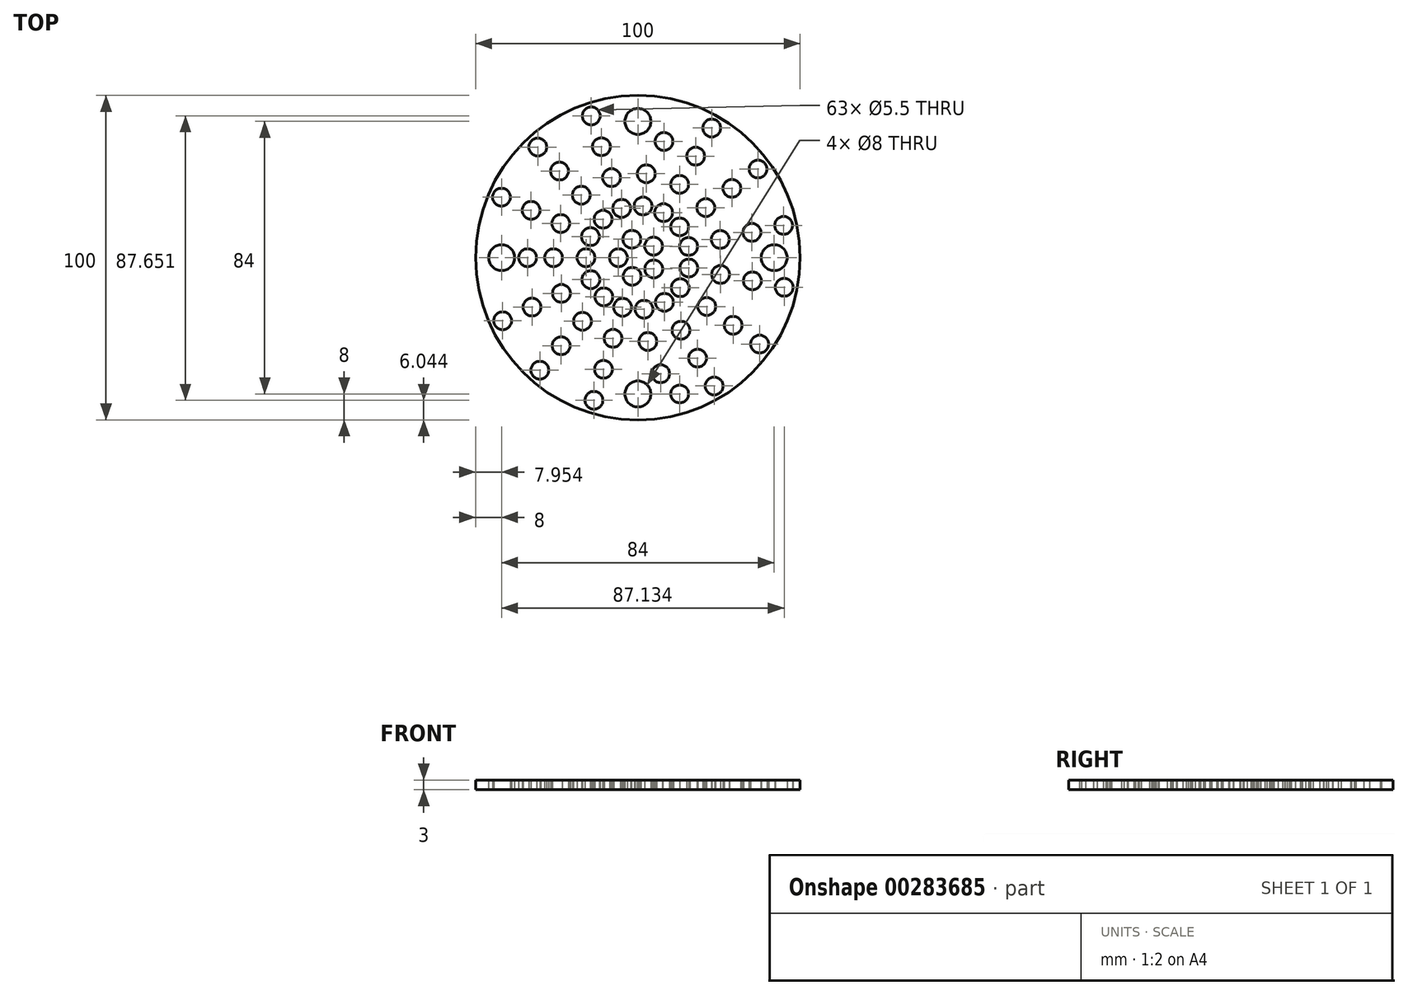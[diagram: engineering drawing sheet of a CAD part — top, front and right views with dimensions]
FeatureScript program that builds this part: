
annotation { "Feature Type Name" : "Feature", "Feature Type Description" : "" }
export const myFeature = defineFeature(function(context is Context, id is Id, definition is map)
    precondition{}
    {
        {
            var Q0;
            Q0=qCreatedBy(makeId("Top.planeOp"),FACE);
            var sketch = newSketch(context, id + "F0", { "sketchPlane" : qUnion([Q0])});
            skCircle(sketch, "E0", {"center": v(0, 0) * mm, "radius": 50 * mm});
            skCircle(sketch, "E1", {"center": v(0, -42) * mm, "radius": 4 * mm});
            skCircle(sketch, "E2.1.0", {"center": v(42, 0) * mm, "radius": 4 * mm});
            skCircle(sketch, "E2.2.0", {"center": v(0, 42) * mm, "radius": 4 * mm});
            skCircle(sketch, "E2.3.0", {"center": v(-42, 0) * mm, "radius": 4 * mm});
            skCircle(sketch, "E3", {"center": v(-6, 0) * mm, "radius": 2.75 * mm});
            skCircle(sketch, "E4.1.0.0", {"center": v(-16, 0) * mm, "radius": 2.75 * mm});
            skCircle(sketch, "E4.2.0.0", {"center": v(-26, 0) * mm, "radius": 2.75 * mm});
            skCircle(sketch, "E4.3.0.0", {"center": v(-34, 0) * mm, "radius": 2.75 * mm});
            skLineSegment(sketch, "E4.direction1", {"start": v(-6, 0) * mm, "end": v(-16, 0) * mm, "construction": true});
            skCircle(sketch, "E5.1.1", {"center": v(-14.62, 6.49) * mm, "radius": 2.75 * mm});
            skCircle(sketch, "E5.1.2", {"center": v(-23.77, 10.55) * mm, "radius": 2.75 * mm});
            skCircle(sketch, "E5.1.3", {"center": v(-32.9, 14.6) * mm, "radius": 2.75 * mm});
            skCircle(sketch, "E5.1.4", {"center": v(-42.05, 18.66) * mm, "radius": 2.75 * mm});
            skCircle(sketch, "E5.2.1", {"center": v(-10.74, 11.86) * mm, "radius": 2.75 * mm});
            skCircle(sketch, "E5.2.2", {"center": v(-17.45, 19.28) * mm, "radius": 2.75 * mm});
            skCircle(sketch, "E5.2.3", {"center": v(-24.16, 26.7) * mm, "radius": 2.75 * mm});
            skCircle(sketch, "E5.2.4", {"center": v(-30.87, 34.1) * mm, "radius": 2.75 * mm});
            skCircle(sketch, "E5.3.0", {"center": v(-1.88, 5.7) * mm, "radius": 2.75 * mm});
            skCircle(sketch, "E5.3.1", {"center": v(-5, 15.2) * mm, "radius": 2.75 * mm});
            skCircle(sketch, "E5.3.2", {"center": v(-8.13, 24.7) * mm, "radius": 2.75 * mm});
            skCircle(sketch, "E5.3.3", {"center": v(-11.25, 34.2) * mm, "radius": 2.75 * mm});
            skCircle(sketch, "E5.3.4", {"center": v(-14.38, 43.7) * mm, "radius": 2.75 * mm});
            skCircle(sketch, "E5.4.1", {"center": v(1.6, 15.92) * mm, "radius": 2.75 * mm});
            skCircle(sketch, "E5.4.2", {"center": v(2.59, 25.87) * mm, "radius": 2.75 * mm});
            skCircle(sketch, "E5.4.3", {"center": v(8.03, 35.82) * mm, "radius": 2.75 * mm});
            skCircle(sketch, "E5.5.1", {"center": v(7.91, 13.9) * mm, "radius": 2.75 * mm});
            skCircle(sketch, "E5.5.2", {"center": v(12.86, 22.6) * mm, "radius": 2.75 * mm});
            skCircle(sketch, "E5.5.3", {"center": v(17.8, 31.29) * mm, "radius": 2.75 * mm});
            skCircle(sketch, "E5.5.4", {"center": v(22.75, 39.98) * mm, "radius": 2.75 * mm});
            skCircle(sketch, "E5.6.0", {"center": v(4.83, 3.56) * mm, "radius": 2.75 * mm});
            skCircle(sketch, "E5.6.1", {"center": v(12.87, 9.5) * mm, "radius": 2.75 * mm});
            skCircle(sketch, "E5.6.2", {"center": v(20.92, 15.44) * mm, "radius": 2.75 * mm});
            skCircle(sketch, "E5.6.3", {"center": v(28.97, 21.38) * mm, "radius": 2.75 * mm});
            skCircle(sketch, "E5.6.4", {"center": v(37.01, 27.32) * mm, "radius": 2.75 * mm});
            skCircle(sketch, "E5.7.1", {"center": v(15.62, 3.46) * mm, "radius": 2.75 * mm});
            skCircle(sketch, "E5.7.2", {"center": v(25.38, 5.63) * mm, "radius": 2.75 * mm});
            skCircle(sketch, "E5.7.3", {"center": v(35.15, 7.8) * mm, "radius": 2.75 * mm});
            skCircle(sketch, "E5.7.4", {"center": v(44.9, 9.96) * mm, "radius": 2.75 * mm});
            skCircle(sketch, "E5.8.1", {"center": v(15.68, -3.17) * mm, "radius": 2.75 * mm});
            skCircle(sketch, "E5.8.2", {"center": v(25.48, -5.15) * mm, "radius": 2.75 * mm});
            skCircle(sketch, "E5.8.3", {"center": v(35.29, -7.13) * mm, "radius": 2.75 * mm});
            skCircle(sketch, "E5.8.4", {"center": v(45.09, -9.11) * mm, "radius": 2.75 * mm});
            skCircle(sketch, "E5.9.0", {"center": v(4.9, -3.47) * mm, "radius": 2.75 * mm});
            skCircle(sketch, "E5.9.1", {"center": v(13.05, -9.26) * mm, "radius": 2.75 * mm});
            skCircle(sketch, "E5.9.2", {"center": v(21.2, -15.05) * mm, "radius": 2.75 * mm});
            skCircle(sketch, "E5.9.3", {"center": v(29.36, -20.83) * mm, "radius": 2.75 * mm});
            skCircle(sketch, "E5.9.4", {"center": v(37.52, -26.62) * mm, "radius": 2.75 * mm});
            skCircle(sketch, "E5.10.1", {"center": v(8.17, -13.76) * mm, "radius": 2.75 * mm});
            skCircle(sketch, "E5.10.2", {"center": v(13.28, -22.35) * mm, "radius": 2.75 * mm});
            skCircle(sketch, "E5.10.3", {"center": v(18.39, -30.95) * mm, "radius": 2.75 * mm});
            skCircle(sketch, "E5.10.4", {"center": v(23.5, -39.55) * mm, "radius": 2.75 * mm});
            skCircle(sketch, "E5.11.1", {"center": v(1.9, -15.89) * mm, "radius": 2.75 * mm});
            skCircle(sketch, "E5.11.2", {"center": v(3.07, -25.82) * mm, "radius": 2.75 * mm});
            skCircle(sketch, "E5.11.3", {"center": v(7, -35.75) * mm, "radius": 2.75 * mm});
            skCircle(sketch, "E5.11.4", {"center": v(12.87, -42) * mm, "radius": 2.75 * mm});
            skCircle(sketch, "E5.12.0", {"center": v(-1.77, -5.73) * mm, "radius": 2.75 * mm});
            skCircle(sketch, "E5.12.1", {"center": v(-4.72, -15.29) * mm, "radius": 2.75 * mm});
            skCircle(sketch, "E5.12.2", {"center": v(-7.66, -24.84) * mm, "radius": 2.75 * mm});
            skCircle(sketch, "E5.12.3", {"center": v(-10.61, -34.4) * mm, "radius": 2.75 * mm});
            skCircle(sketch, "E5.12.4", {"center": v(-13.56, -43.96) * mm, "radius": 2.75 * mm});
            skCircle(sketch, "E5.13.1", {"center": v(-10.51, -12.06) * mm, "radius": 2.75 * mm});
            skCircle(sketch, "E5.13.2", {"center": v(-17.08, -19.6) * mm, "radius": 2.75 * mm});
            skCircle(sketch, "E5.13.3", {"center": v(-23.65, -27.14) * mm, "radius": 2.75 * mm});
            skCircle(sketch, "E5.13.4", {"center": v(-30.22, -34.68) * mm, "radius": 2.75 * mm});
            skCircle(sketch, "E5.14.1", {"center": v(-14.5, -6.76) * mm, "radius": 2.75 * mm});
            skCircle(sketch, "E5.14.2", {"center": v(-23.56, -10.99) * mm, "radius": 2.75 * mm});
            skCircle(sketch, "E5.14.3", {"center": v(-32.63, -15.21) * mm, "radius": 2.75 * mm});
            skCircle(sketch, "E5.14.4", {"center": v(-41.7, -19.44) * mm, "radius": 2.75 * mm});
            skLineSegment(sketch, "E5.anchor1", {"start": v(0, 0) * mm, "end": v(-6, 0) * mm, "construction": true});
            skLineSegment(sketch, "E5.anchor2", {"start": v(0, 0) * mm, "end": v(-5.44, -2.54) * mm, "construction": true});
            skSolve(sketch);
        }
        {
            var Q0;
            Q0=makeQuery(id+"F0.imprint","IMPRINT",FACE,{"disambiguationData":[TD([[makeQuery(id+"F0.imprint","IMPRINT",EDGE,{"derivedFrom":sQuery(id+"F0.wireOp",EDGE,"E0")}),1.0]])]});
            extrude(context, id + "F1", {"entities" : qUnion([Q0]), "depth" : 3 * mm});
        }
    });
